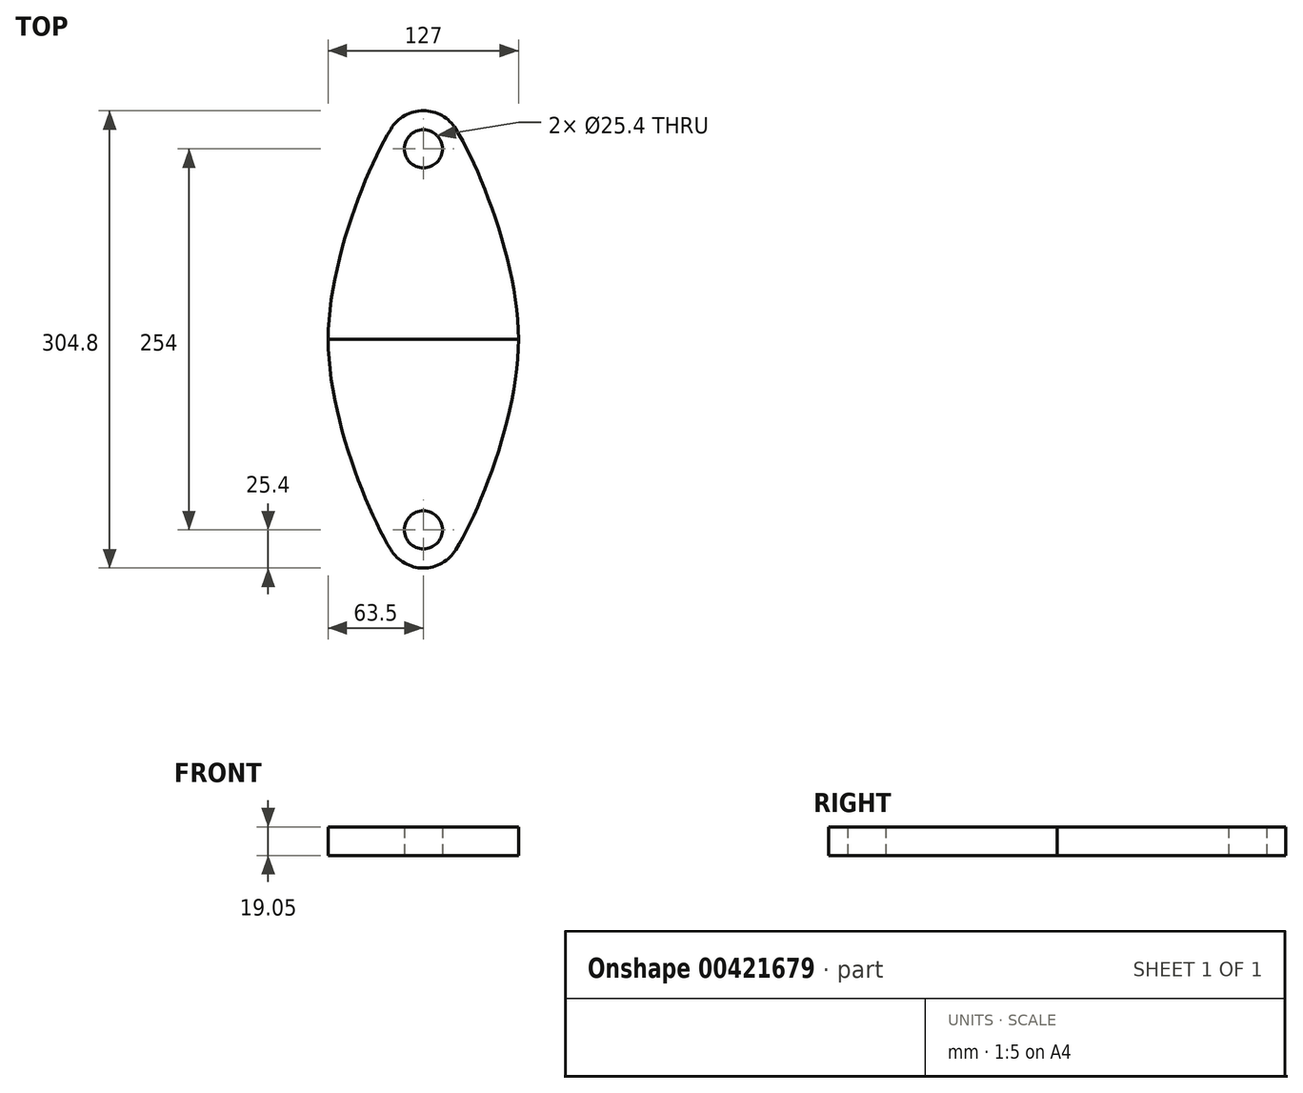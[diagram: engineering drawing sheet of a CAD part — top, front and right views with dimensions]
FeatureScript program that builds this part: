
annotation { "Feature Type Name" : "Feature", "Feature Type Description" : "" }
export const myFeature = defineFeature(function(context is Context, id is Id, definition is map)
    precondition{}
    {
        {
            var Q0;
            Q0=qCreatedBy(makeId("Top.planeOp"),FACE);
            var sketch = newSketch(context, id + "F0", { "sketchPlane" : qUnion([Q0])});
            skCircle(sketch, "E0", {"center": v(0, 127) * mm, "radius": 12.7 * mm});
            skLineSegment(sketch, "E1", {"start": v(0, 0) * mm, "end": v(63.5, 0) * mm});
            skArc(sketch, "E2", {"start": v(0, 152.4) * mm, "mid": v(12.44, 149.14) * mm, "end": v(21.7, 140.2) * mm});
            skFitSpline(sketch, "E3", {"points": [v(21.7, 140.2) * mm, v(63.5, 0) * mm], "startDerivative": vector(51.68, -84.9) * mm, "endDerivative": vector(0, -145.93) * mm});
            skLineSegment(sketch, "E4", {"start": v(21.7, 140.2) * mm, "end": v(38.92, 111.9) * mm, "construction": true});
            skArc(sketch, "E5.MirrorCS", {"start": v(0, 152.4) * mm, "mid": v(-12.44, 149.14) * mm, "end": v(-21.7, 140.2) * mm});
            skFitSpline(sketch, "E6.MirrorCS", {"points": [v(-21.7, 140.2) * mm, v(-63.5, 0) * mm], "startDerivative": vector(-51.68, -84.9) * mm, "endDerivative": vector(0, -145.93) * mm});
            skLineSegment(sketch, "E7.MirrorCS", {"start": v(0, 0) * mm, "end": v(-63.5, 0) * mm});
            skSolve(sketch);
        }
        {
            var Q0;
            Q0=makeQuery(id+"F0.imprint","IMPRINT",FACE,{"disambiguationData":[TD([[makeQuery(id+"F0.imprint","IMPRINT",EDGE,{"derivedFrom":sQuery(id+"F0.wireOp",EDGE,"E0")}),-1.0]])]});
            var Q1;
            Q1=makeQuery(id+"F0.imprint","IMPRINT",FACE,{"disambiguationData":[TD([[makeQuery(id+"F0.imprint","IMPRINT",EDGE,{"derivedFrom":sQuery(id+"F0.wireOp",EDGE,"1a9d1462-988f-457c-b9a2-63156555b0d20.MirrorCS")}),-1.0]])]});
            extrude(context, id + "F1", {"entities" : qUnion([Q0, Q1]), "depth" : 19.05 * mm});
        }
        {
            var Q0;
            Q0=makeQuery(id+"F1.opExtrude","SWEPT_BODY",BODY,{"disambiguationData":[OSD([sQuery(id+"F0.wireOp",EDGE,"E0"),sQuery(id+"F0.wireOp",EDGE,"E1"),sQuery(id+"F0.wireOp",EDGE,"E2"),sQuery(id+"F0.wireOp",EDGE,"E3"),sQuery(id+"F0.wireOp",EDGE,"E5.MirrorCS"),sQuery(id+"F0.wireOp",EDGE,"E6.MirrorCS"),sQuery(id+"F0.wireOp",EDGE,"E7.MirrorCS")])]});
            var Q1;
            Q1=qCreatedBy(makeId("Front.planeOp"),FACE);
            mirror(context, id + "F2", {"entities" : qUnion([Q0]), "mirrorPlane" : qUnion([Q1])});
        }
    });
